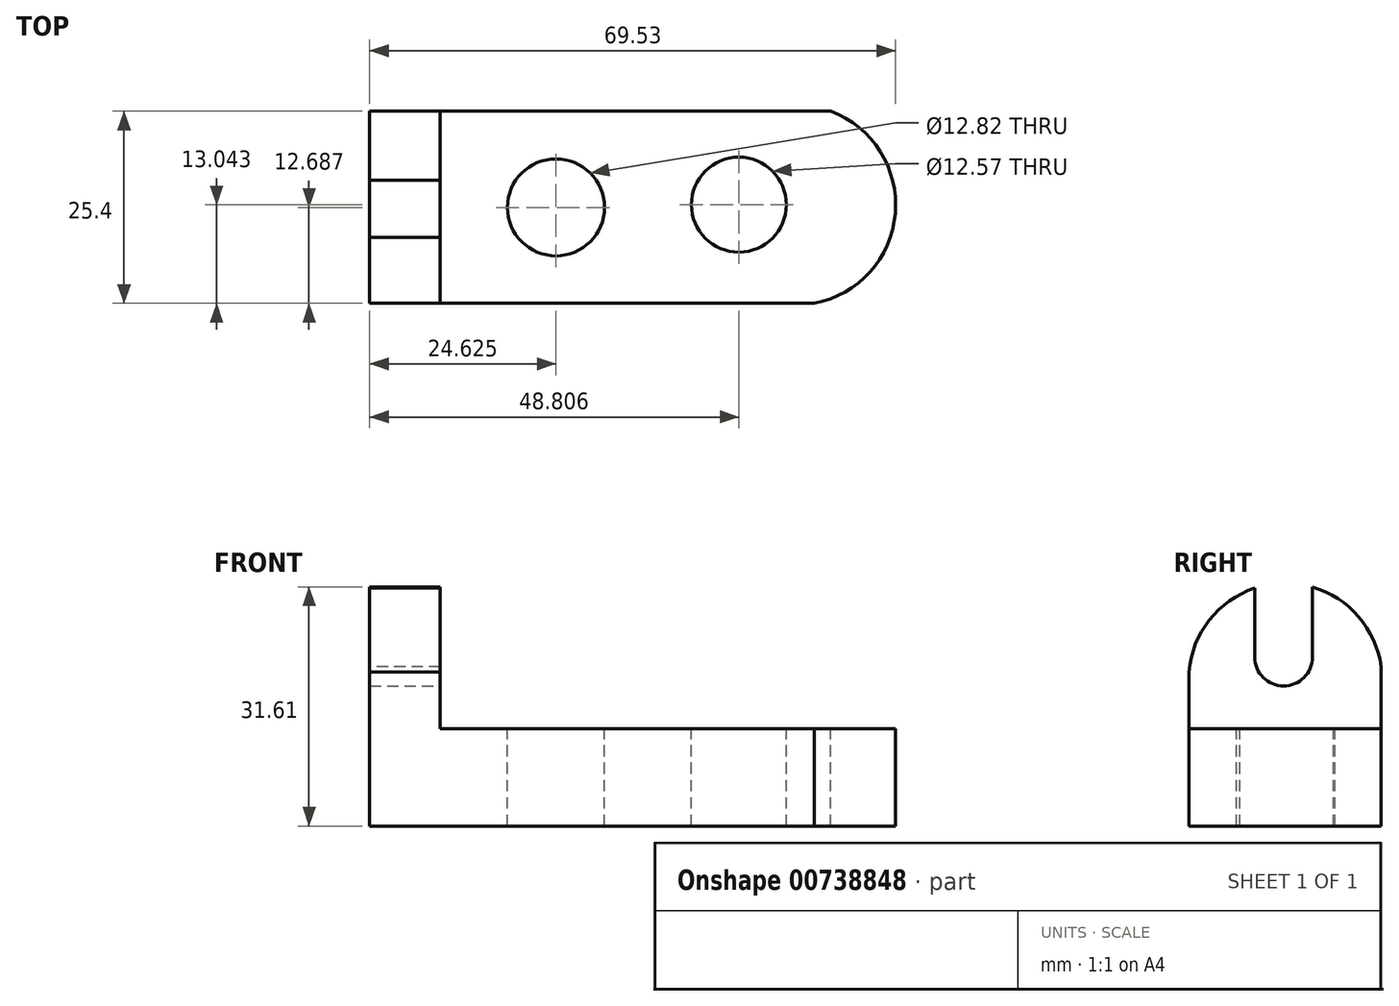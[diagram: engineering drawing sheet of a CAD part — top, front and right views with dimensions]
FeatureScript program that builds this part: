
annotation { "Feature Type Name" : "Feature", "Feature Type Description" : "" }
export const myFeature = defineFeature(function(context is Context, id is Id, definition is map)
    precondition{}
    {
        {
            var Q0;
            Q0=qCreatedBy(makeId("Front.planeOp"),FACE);
            var sketch = newSketch(context, id + "F0", { "sketchPlane" : qUnion([Q0])});
            skLineSegment(sketch, "E0", {"start": v(0, 0) * mm, "end": v(69.6, 0) * mm});
            skLineSegment(sketch, "E1", {"start": v(69.6, 0) * mm, "end": v(69.6, 12.9) * mm});
            skLineSegment(sketch, "E2", {"start": v(69.6, 12.9) * mm, "end": v(9.33, 12.9) * mm});
            skLineSegment(sketch, "E3", {"start": v(9.33, 12.9) * mm, "end": v(9.33, 31.92) * mm});
            skLineSegment(sketch, "E4", {"start": v(9.33, 31.92) * mm, "end": v(0, 31.92) * mm});
            skLineSegment(sketch, "E5", {"start": v(0, 31.92) * mm, "end": v(0, 0) * mm});
            skSolve(sketch);
        }
        {
            var Q0;
            Q0 = qSketchRegion(id + "F0", true);
            extrude(context, id + "F1", {"entities" : qUnion([Q0]), "depth" : 25.4 * mm, "offsetDistance" : 25.4 * mm});
        }
        {
            var Q0;
            Q0=makeQuery(id+"F1.opExtrude","SWEPT_FACE",FACE,{"disambiguationData":[OSD([sQuery(id+"F0.wireOp",EDGE,"E2")])]});
            var sketch = newSketch(context, id + "F2", { "sketchPlane" : qUnion([Q0])});
            skCircle(sketch, "E6", {"center": v(24.63, -12.71) * mm, "radius": 6.41 * mm});
            skCircle(sketch, "E7", {"center": v(48.8, -12.36) * mm, "radius": 6.29 * mm});
            skSolve(sketch);
        }
        {
            var Q0;
            Q0=makeQuery(id+"F2.imprint","IMPRINT",FACE,{"disambiguationData":[TD([[makeQuery(id+"F2.imprint","IMPRINT",EDGE,{"derivedFrom":sQuery(id+"F2.wireOp",EDGE,"E7")}),1.0]])]});
            var Q1;
            Q1=makeQuery(id+"F2.imprint","IMPRINT",FACE,{"disambiguationData":[TD([[makeQuery(id+"F2.imprint","IMPRINT",EDGE,{"derivedFrom":sQuery(id+"F2.wireOp",EDGE,"E6")}),1.0]])]});
            extrude(context, id + "F3", {"entities" : qUnion([Q0, Q1]), "operationType" : NewBodyOperationType.REMOVE, "endBound" : BoundingType.THROUGH_ALL, "oppositeDirection" : true, "depth" : 25.4 * mm, "offsetDistance" : 25.4 * mm});
        }
        {
            var Q0;
            Q0=makeQuery(id+"F1.opExtrude","SWEPT_FACE",FACE,{"disambiguationData":[OSD([sQuery(id+"F0.wireOp",EDGE,"E2")])]});
            var sketch = newSketch(context, id + "F4", { "sketchPlane" : qUnion([Q0])});
            skArc(sketch, "E8", {"start": v(53.78, -25.4) * mm, "mid": v(69.48, -11.3) * mm, "end": v(51.65, 0) * mm});
            skSolve(sketch);
        }
        {
            var Q0;
            {var subQ1=sQuery(id+"F0.wireOp",EDGE,"E2");var subQ6=makeQuery(id+"F1.opExtrude","SWEPT_EDGE",EDGE,{"disambiguationData":[OSD([sQuery(id+"F0.wireOp",EDGE,"E1"),subQ1])]});Q0=makeQuery(id+"F4.imprint","IMPRINT",FACE,{"disambiguationData":[TD([[makeQuery(id+"F4.imprint","IMPRINT",EDGE,{"derivedFrom":subQ6}),1.0]])]});}
            extrude(context, id + "F5", {"entities" : qUnion([Q0]), "operationType" : NewBodyOperationType.REMOVE, "endBound" : BoundingType.THROUGH_ALL, "oppositeDirection" : true, "depth" : 25.4 * mm, "offsetDistance" : 25.4 * mm});
        }
        {
            var Q0;
            Q0=makeQuery(id+"F1.opExtrude","SWEPT_FACE",FACE,{"disambiguationData":[OSD([sQuery(id+"F0.wireOp",EDGE,"E5")])]});
            var sketch = newSketch(context, id + "F6", { "sketchPlane" : qUnion([Q0])});
            skArc(sketch, "E9", {"start": v(25.4, 20.36) * mm, "mid": v(13.02, 32.11) * mm, "end": v(0, 21.07) * mm});
            skSolve(sketch);
        }
        {
            var Q0;
            {var subQ0=sQuery(id+"F6.wireOp",EDGE,"E9");var subQ1=sQuery(id+"F0.wireOp",EDGE,"E5");var subQ2=makeQuery(id+"F1.opExtrude","CAP_EDGE",EDGE,{"disambiguationData":[OSD([subQ1])],"isStart":true});var subQ3=makeQuery(id+"F6.imprint","INTERSECT",VERTEX,{"derivedFrom":[subQ2,subQ0]});Q0=makeQuery(id+"F6.imprint","IMPRINT",FACE,{"disambiguationData":[TD([[makeQuery(id+"F6.imprint","IMPRINT",EDGE,{"disambiguationData":[TD([[subQ3,1.0]])],"derivedFrom":subQ0}),-1.0]])]});}
            var Q1;
            {var subQ0=sQuery(id+"F6.wireOp",EDGE,"E9");var subQ1=sQuery(id+"F0.wireOp",EDGE,"E5");var subQ2=makeQuery(id+"F1.opExtrude","CAP_EDGE",EDGE,{"disambiguationData":[OSD([subQ1])],"isStart":false});var subQ3=makeQuery(id+"F6.imprint","INTERSECT",VERTEX,{"derivedFrom":[subQ2,subQ0]});Q1=makeQuery(id+"F6.imprint","IMPRINT",FACE,{"disambiguationData":[TD([[makeQuery(id+"F6.imprint","IMPRINT",EDGE,{"disambiguationData":[TD([[subQ3,-1.0]])],"derivedFrom":subQ0}),-1.0]])]});}
            extrude(context, id + "F7", {"entities" : qUnion([Q0, Q1]), "operationType" : NewBodyOperationType.REMOVE, "endBound" : BoundingType.THROUGH_ALL, "oppositeDirection" : true, "depth" : 25.4 * mm, "offsetDistance" : 25.4 * mm});
        }
        {
            var Q0;
            Q0=makeQuery(id+"F1.opExtrude","SWEPT_FACE",FACE,{"disambiguationData":[OSD([sQuery(id+"F0.wireOp",EDGE,"E3")])]});
            var sketch = newSketch(context, id + "F8", { "sketchPlane" : qUnion([Q0])});
            skSolve(sketch);
        }
        {
            var Q0;
            {var subQ0=sQuery(id+"F0.wireOp",EDGE,"E3");Q0=makeQuery(id+"F8.imprint","IMPRINT",FACE,{"disambiguationData":[TD([[makeQuery(id+"F8.imprint","IMPRINT",EDGE,{"derivedFrom":makeQuery(id+"F1.opExtrude","CAP_EDGE",EDGE,{"disambiguationData":[OSD([subQ0])],"isStart":true})}),1.0]])]});}
            var sketch = newSketch(context, id + "F9", { "sketchPlane" : qUnion([Q0])});
            skCircle(sketch, "E10", {"center": v(-12.9, 22.31) * mm, "radius": 3.8 * mm});
            skLineSegment(sketch, "E11", {"start": v(-16.7, 22.31) * mm, "end": v(-16.7, 31.92) * mm});
            skLineSegment(sketch, "E12", {"start": v(-9.09, 22.31) * mm, "end": v(-9.09, 31.74) * mm});
            skSolve(sketch);
        }
        {
            var Q0;
            {var subQ5=sQuery(id+"F0.wireOp",EDGE,"E4");var subQ7=sQuery(id+"F0.wireOp",EDGE,"E3");var subQ15=makeQuery(id+"F8.imprint","IMPRINT",EDGE,{"derivedFrom":makeQuery(id+"F1.opExtrude","SWEPT_EDGE",EDGE,{"disambiguationData":[OSD([subQ7,subQ5])]})});Q0=makeQuery(id+"F9.imprint","IMPRINT",FACE,{"disambiguationData":[TD([[makeQuery(id+"F9.imprint","IMPRINT",EDGE,{"derivedFrom":subQ15}),-1.0]])]});}
            var Q1;
            {var subQ0=sQuery(id+"F9.wireOp",EDGE,"E10");var subQ1=makeQuery(id+"F9.imprint","INTERSECT",VERTEX,{"derivedFrom":[subQ0,sQuery(id+"F9.wireOp",EDGE,"E11")]});Q1=makeQuery(id+"F9.imprint","IMPRINT",FACE,{"disambiguationData":[TD([[makeQuery(id+"F9.imprint","IMPRINT",EDGE,{"disambiguationData":[TD([[subQ1,1.0]])],"derivedFrom":subQ0}),1.0]])]});}
            extrude(context, id + "F10", {"entities" : qUnion([Q0, Q1]), "operationType" : NewBodyOperationType.REMOVE, "endBound" : BoundingType.THROUGH_ALL, "oppositeDirection" : true, "depth" : 25.4 * mm, "offsetDistance" : 25.4 * mm});
        }
    });
